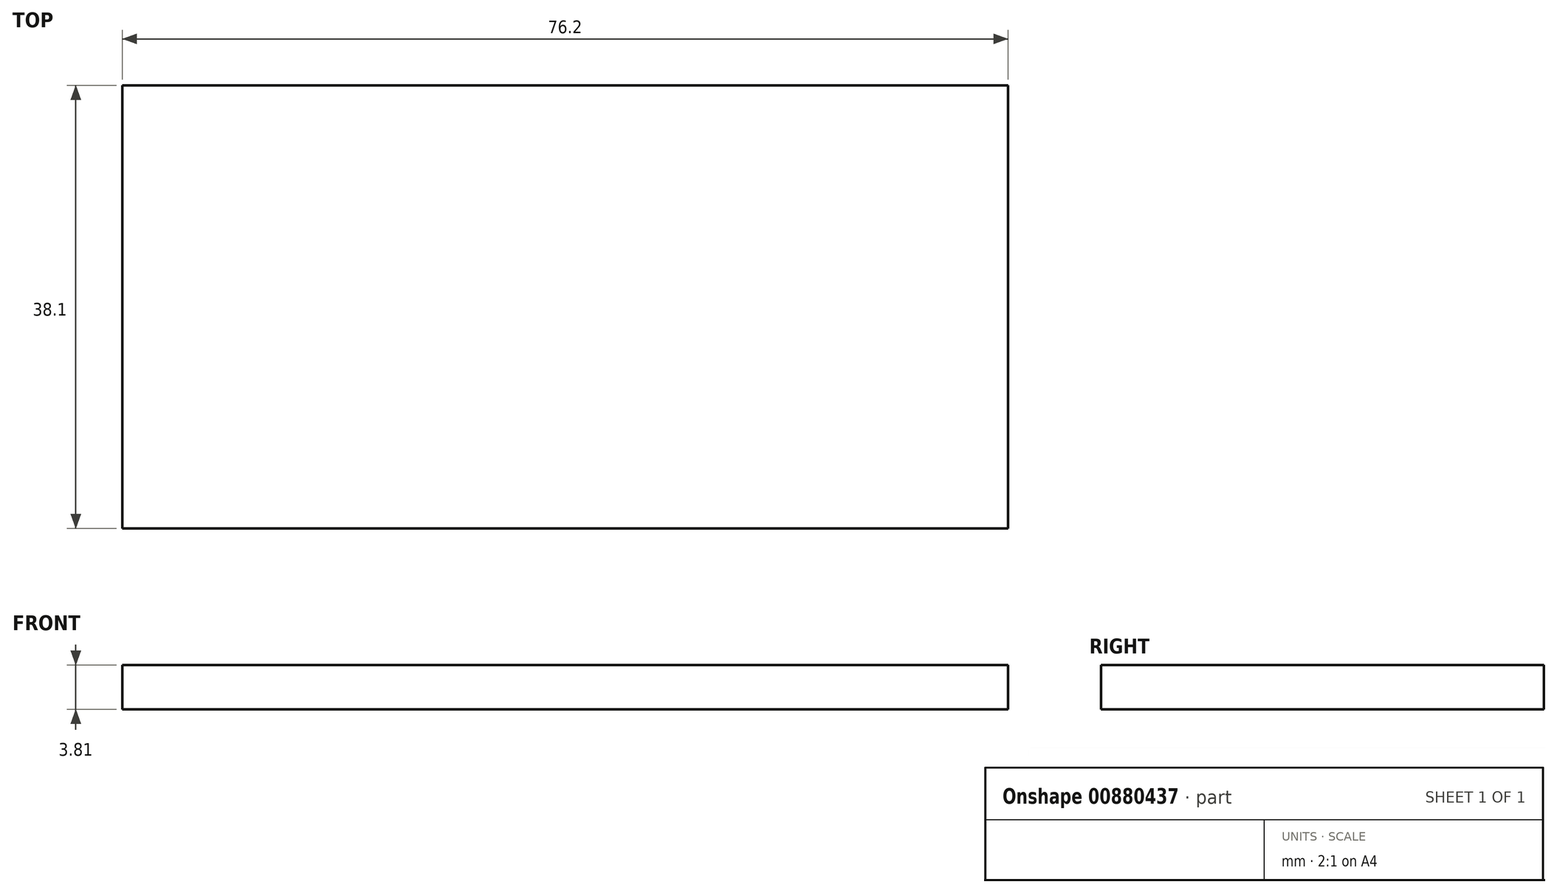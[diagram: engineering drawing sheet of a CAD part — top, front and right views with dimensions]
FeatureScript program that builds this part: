
annotation { "Feature Type Name" : "Feature", "Feature Type Description" : "" }
export const myFeature = defineFeature(function(context is Context, id is Id, definition is map)
    precondition{}
    {
        {
            var Q0;
            Q0=qCreatedBy(makeId("Top.planeOp"),FACE);
            var sketch = newSketch(context, id + "F0", { "sketchPlane" : qUnion([Q0])});
            skLineSegment(sketch, "E0.bottom", {"start": v(38.1, 19.05) * mm, "end": v(-38.1, 19.05) * mm});
            skLineSegment(sketch, "E0.top", {"start": v(38.1, -19.05) * mm, "end": v(-38.1, -19.05) * mm});
            skLineSegment(sketch, "E0.left", {"start": v(38.1, 19.05) * mm, "end": v(38.1, -19.05) * mm});
            skPoint(sketch, "E0.middle", {"position": v(0, 0) * mm});
            skLineSegment(sketch, "E1", {"start": v(38.1, 14.29) * mm, "end": v(38.1, -14.29) * mm, "construction": true});
            skPoint(sketch, "E2", {"position": v(-33.34, 14.29) * mm});
            skPoint(sketch, "E3", {"position": v(-33.34, -14.29) * mm});
            skPoint(sketch, "E4", {"position": v(33.34, -14.29) * mm});
            skPoint(sketch, "E5", {"position": v(33.34, 14.29) * mm});
            skLineSegment(sketch, "E6", {"start": v(-38.1, -19.05) * mm, "end": v(-38.1, 19.05) * mm});
            skSolve(sketch);
        }
        {
            var Q0;
            Q0=makeQuery(id+"F0.imprint","IMPRINT",FACE,{"disambiguationData":[TD([[makeQuery(id+"F0.imprint","IMPRINT",EDGE,{"derivedFrom":sQuery(id+"F0.wireOp",EDGE,"E0.bottom")}),1.0]])]});
            extrude(context, id + "F1", {"entities" : qUnion([Q0]), "depth" : 3.8 * mm, "offsetDistance" : 25.4 * mm});
        }
    });
